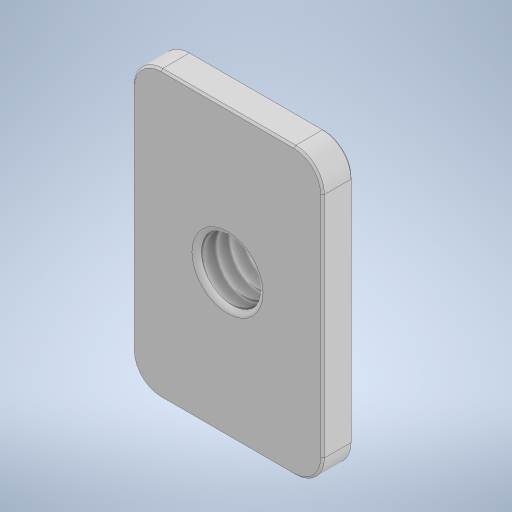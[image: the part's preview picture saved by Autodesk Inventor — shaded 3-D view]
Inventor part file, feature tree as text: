
AUTODESK INVENTOR PART (.ipt)
format: ipt  version: 2024 (Build 280153000, 153)  size: 287,232 bytes
history: native  units: mm
features: fillet x3, sketch x3, extrude x2, chamfer x2, hole x1
ambient origin geometry x8: Origin, YZ Plane, XZ Plane, XY Plane, X Axis, Y Axis, Z Axis, Center Point
bodies: Solid1 (feature_tree)
feature tree (11):
  extrude  "Extrusion1"  Depth=15.0mm
  extrude  "Extrusion2"  Depth=0.25mm
  fillet  "Fillet1"  Radius=1.4mm
  fillet  "Fillet2"  Radius=0.25mm
  hole  "Hole1"  [1 undecoded]
  fillet  "Fillet3"  Radius=0.1mm
  chamfer  "Chamfer1"  Distance=0.1mm Angle=45.0deg
  chamfer  "Chamfer2"  [1 undecoded]
  sketch  "Sketch1"  dims[d0=10.0mm d1=15.0mm]
  sketch  "Sketch2"  dims[d2=1.6mm d3=0.0mm d4=6.9mm d5=1.4mm d6=0.0mm d7=0.25mm]
  sketch  "Sketch3"  dims[d8=1.5mm d9=3.242mm d10=8.0mm d11=4.0mm d12=2.0mm d13=90.0deg d14=14.2mm d15=150.0deg d16=0.25mm d17=0.1mm d18=2.0mm d19=45.0deg d20=0.1mm d21=2.0mm d22=45.0deg]
note: 2 required parameter values undecoded (feature->parameter linkage not recoverable at this tier; creation-order binding heuristic only, values carry confidence <= 0.55)
